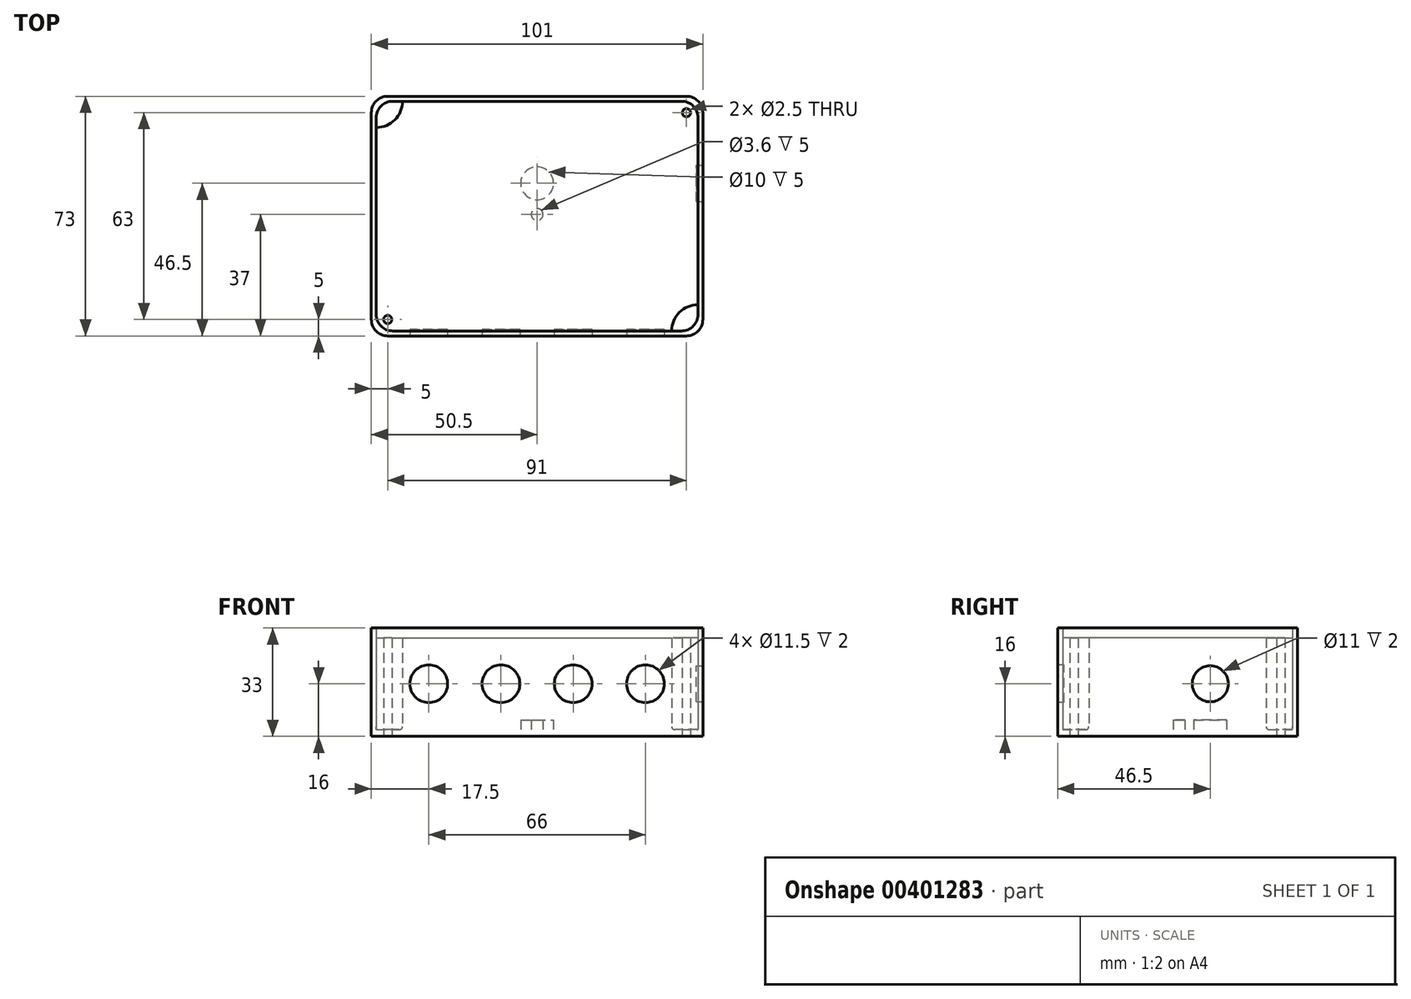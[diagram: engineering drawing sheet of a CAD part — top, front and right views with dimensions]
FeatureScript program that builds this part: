
annotation { "Feature Type Name" : "Feature", "Feature Type Description" : "" }
export const myFeature = defineFeature(function(context is Context, id is Id, definition is map)
    precondition{}
    {
        {
            var Q0;
            Q0=qCreatedBy(makeId("Top.planeOp"),FACE);
            var sketch = newSketch(context, id + "F0", { "sketchPlane" : qUnion([Q0])});
            skLineSegment(sketch, "E0.bottom", {"start": v(49, -45) * mm, "end": v(-49, -45) * mm});
            skLineSegment(sketch, "E0.top", {"start": v(49, 25) * mm, "end": v(-49, 25) * mm});
            skLineSegment(sketch, "E0.left", {"start": v(49, -45) * mm, "end": v(49, 25) * mm});
            skLineSegment(sketch, "E0.right", {"start": v(-49, -45) * mm, "end": v(-49, 25) * mm});
            skLineSegment(sketch, "E1.bottom", {"start": v(-50.5, 26.5) * mm, "end": v(50.5, 26.5) * mm});
            skLineSegment(sketch, "E1.top", {"start": v(-50.5, -46.5) * mm, "end": v(50.5, -46.5) * mm});
            skLineSegment(sketch, "E1.left", {"start": v(-50.5, 26.5) * mm, "end": v(-50.5, -46.5) * mm});
            skLineSegment(sketch, "E1.right", {"start": v(50.5, 26.5) * mm, "end": v(50.5, -46.5) * mm});
            skArc(sketch, "E2", {"start": v(-41, 25) * mm, "mid": v(-43.34, 19.34) * mm, "end": v(-49, 17) * mm});
            skArc(sketch, "E3.MirrorCS", {"start": v(41, 25) * mm, "mid": v(43.34, 19.34) * mm, "end": v(49, 17) * mm});
            skLineSegment(sketch, "E4", {"start": v(-73.7, -10) * mm, "end": v(81.7, -10) * mm, "construction": true});
            skPoint(sketch, "E5", {"position": v(49, -10) * mm});
            skArc(sketch, "E6.MirrorCS", {"start": v(-41, -45) * mm, "mid": v(-43.34, -39.34) * mm, "end": v(-49, -37) * mm});
            skArc(sketch, "E7.MirrorCS", {"start": v(41, -45) * mm, "mid": v(43.34, -39.34) * mm, "end": v(49, -37) * mm});
            skCircle(sketch, "E8", {"center": v(-45.5, 21.5) * mm, "radius": 1.25 * mm});
            skCircle(sketch, "E9.MirrorC", {"center": v(45.5, 21.5) * mm, "radius": 1.25 * mm});
            skCircle(sketch, "E10.MirrorC", {"center": v(45.5, -41.5) * mm, "radius": 1.25 * mm});
            skCircle(sketch, "E11.MirrorC", {"center": v(-45.5, -41.5) * mm, "radius": 1.25 * mm});
            skSolve(sketch);
        }
        {
            var Q0;
            Q0=makeQuery(id+"F0.imprint","IMPRINT",FACE,{"disambiguationData":[TD([[makeQuery(id+"F0.imprint","IMPRINT",EDGE,{"derivedFrom":sQuery(id+"F0.wireOp",EDGE,"E0.bottom")}),-1.0]])]});
            var Q1;
            Q1=makeQuery(id+"F0.imprint","IMPRINT",FACE,{"disambiguationData":[TD([[makeQuery(id+"F0.imprint","IMPRINT",EDGE,{"derivedFrom":sQuery(id+"F0.wireOp",EDGE,"Ogz6Qpz2-tZH1-9vVJ-3AU5-A4KMQRxO9mfY.bottom")}),1.0]])]});
            var Q2;
            {var subQ0=sQuery(id+"F0.wireOp",EDGE,"e8d4081c-b40e-46aa-b9e9-f96a25c7d6070.MirrorC");var subQ1=sQuery(id+"F0.wireOp",EDGE,"usMzGdrf-JS18-KNfs-daDR-j57PrwHz9FGL.top");var subQ2=makeQuery(id+"F0.imprint","INTERSECT",VERTEX,{"derivedFrom":[subQ1,subQ0]});Q2=makeQuery(id+"F0.imprint","IMPRINT",FACE,{"disambiguationData":[TD([[makeQuery(id+"F0.imprint","IMPRINT",EDGE,{"disambiguationData":[TD([[subQ2,-1.0]])],"derivedFrom":subQ1}),-1.0]])]});}
            var Q3;
            {var subQ0=sQuery(id+"F0.wireOp",EDGE,"usMzGdrf-JS18-KNfs-daDR-j57PrwHz9FGL.right");var subQ1=sQuery(id+"F0.wireOp",EDGE,"usMzGdrf-JS18-KNfs-daDR-j57PrwHz9FGL.top");var subQ2=makeQuery(id+"F0.imprint","INTERSECT",VERTEX,{"derivedFrom":[subQ1,subQ0]});Q3=makeQuery(id+"F0.imprint","IMPRINT",FACE,{"disambiguationData":[TD([[makeQuery(id+"F0.imprint","IMPRINT",EDGE,{"disambiguationData":[TD([[subQ2,1.0]])],"derivedFrom":subQ1}),-1.0]])]});}
            var Q4;
            {var subQ0=sQuery(id+"F0.wireOp",EDGE,"e8d4081c-b40e-46aa-b9e9-f96a25c7d6070.MirrorC");var subQ1=sQuery(id+"F0.wireOp",EDGE,"usMzGdrf-JS18-KNfs-daDR-j57PrwHz9FGL.top");var subQ2=makeQuery(id+"F0.imprint","INTERSECT",VERTEX,{"derivedFrom":[subQ1,subQ0]});Q4=makeQuery(id+"F0.imprint","IMPRINT",FACE,{"disambiguationData":[TD([[makeQuery(id+"F0.imprint","IMPRINT",EDGE,{"disambiguationData":[TD([[subQ2,-1.0]])],"derivedFrom":subQ1}),1.0]])]});}
            var Q5;
            {var subQ0=sQuery(id+"F0.wireOp",EDGE,"usMzGdrf-JS18-KNfs-daDR-j57PrwHz9FGL.right");var subQ1=sQuery(id+"F0.wireOp",EDGE,"usMzGdrf-JS18-KNfs-daDR-j57PrwHz9FGL.top");var subQ2=makeQuery(id+"F0.imprint","INTERSECT",VERTEX,{"derivedFrom":[subQ1,subQ0]});Q5=makeQuery(id+"F0.imprint","IMPRINT",FACE,{"disambiguationData":[TD([[makeQuery(id+"F0.imprint","IMPRINT",EDGE,{"disambiguationData":[TD([[subQ2,1.0]])],"derivedFrom":subQ1}),1.0]])]});}
            var Q6;
            {var subQ0=sQuery(id+"F0.wireOp",EDGE,"usMzGdrf-JS18-KNfs-daDR-j57PrwHz9FGL.right");var subQ1=sQuery(id+"F0.wireOp",EDGE,"usMzGdrf-JS18-KNfs-daDR-j57PrwHz9FGL.bottom");var subQ2=makeQuery(id+"F0.imprint","INTERSECT",VERTEX,{"derivedFrom":[subQ1,subQ0]});Q6=makeQuery(id+"F0.imprint","IMPRINT",FACE,{"disambiguationData":[TD([[makeQuery(id+"F0.imprint","IMPRINT",EDGE,{"disambiguationData":[TD([[subQ2,1.0]])],"derivedFrom":subQ1}),-1.0]])]});}
            var Q7;
            {var subQ0=sQuery(id+"F0.wireOp",EDGE,"44b00ebe-043b-4d1d-bd37-5f580f74e6f70.MirrorC");var subQ1=sQuery(id+"F0.wireOp",EDGE,"usMzGdrf-JS18-KNfs-daDR-j57PrwHz9FGL.bottom");var subQ2=makeQuery(id+"F0.imprint","INTERSECT",VERTEX,{"derivedFrom":[subQ1,subQ0]});Q7=makeQuery(id+"F0.imprint","IMPRINT",FACE,{"disambiguationData":[TD([[makeQuery(id+"F0.imprint","IMPRINT",EDGE,{"disambiguationData":[TD([[subQ2,-1.0]])],"derivedFrom":subQ1}),-1.0]])]});}
            var Q8;
            {var subQ0=sQuery(id+"F0.wireOp",EDGE,"44b00ebe-043b-4d1d-bd37-5f580f74e6f70.MirrorC");var subQ1=sQuery(id+"F0.wireOp",EDGE,"usMzGdrf-JS18-KNfs-daDR-j57PrwHz9FGL.bottom");var subQ2=makeQuery(id+"F0.imprint","INTERSECT",VERTEX,{"derivedFrom":[subQ1,subQ0]});Q8=makeQuery(id+"F0.imprint","IMPRINT",FACE,{"disambiguationData":[TD([[makeQuery(id+"F0.imprint","IMPRINT",EDGE,{"disambiguationData":[TD([[subQ2,-1.0]])],"derivedFrom":subQ1}),1.0]])]});}
            var Q9;
            {var subQ0=sQuery(id+"F0.wireOp",EDGE,"usMzGdrf-JS18-KNfs-daDR-j57PrwHz9FGL.right");var subQ1=sQuery(id+"F0.wireOp",EDGE,"usMzGdrf-JS18-KNfs-daDR-j57PrwHz9FGL.bottom");var subQ2=makeQuery(id+"F0.imprint","INTERSECT",VERTEX,{"derivedFrom":[subQ1,subQ0]});Q9=makeQuery(id+"F0.imprint","IMPRINT",FACE,{"disambiguationData":[TD([[makeQuery(id+"F0.imprint","IMPRINT",EDGE,{"disambiguationData":[TD([[subQ2,1.0]])],"derivedFrom":subQ1}),1.0]])]});}
            var Q10;
            {var subQ0=sQuery(id+"F0.wireOp",EDGE,"GhtEGfij-EbOE-fe6g-4XEu-vHL9JId5yvzA");var subQ1=sQuery(id+"F0.wireOp",EDGE,"usMzGdrf-JS18-KNfs-daDR-j57PrwHz9FGL.top");var subQ2=makeQuery(id+"F0.imprint","INTERSECT",VERTEX,{"derivedFrom":[subQ1,subQ0]});Q10=makeQuery(id+"F0.imprint","IMPRINT",FACE,{"disambiguationData":[TD([[makeQuery(id+"F0.imprint","IMPRINT",EDGE,{"disambiguationData":[TD([[subQ2,-1.0]])],"derivedFrom":subQ1}),-1.0]])]});}
            var Q11;
            {var subQ0=sQuery(id+"F0.wireOp",EDGE,"usMzGdrf-JS18-KNfs-daDR-j57PrwHz9FGL.left");var subQ1=sQuery(id+"F0.wireOp",EDGE,"usMzGdrf-JS18-KNfs-daDR-j57PrwHz9FGL.top");var subQ2=makeQuery(id+"F0.imprint","INTERSECT",VERTEX,{"derivedFrom":[subQ1,subQ0]});Q11=makeQuery(id+"F0.imprint","IMPRINT",FACE,{"disambiguationData":[TD([[makeQuery(id+"F0.imprint","IMPRINT",EDGE,{"disambiguationData":[TD([[subQ2,-1.0]])],"derivedFrom":subQ1}),-1.0]])]});}
            var Q12;
            {var subQ0=sQuery(id+"F0.wireOp",EDGE,"GhtEGfij-EbOE-fe6g-4XEu-vHL9JId5yvzA");var subQ1=sQuery(id+"F0.wireOp",EDGE,"usMzGdrf-JS18-KNfs-daDR-j57PrwHz9FGL.top");var subQ2=makeQuery(id+"F0.imprint","INTERSECT",VERTEX,{"derivedFrom":[subQ1,subQ0]});Q12=makeQuery(id+"F0.imprint","IMPRINT",FACE,{"disambiguationData":[TD([[makeQuery(id+"F0.imprint","IMPRINT",EDGE,{"disambiguationData":[TD([[subQ2,-1.0]])],"derivedFrom":subQ1}),1.0]])]});}
            var Q13;
            {var subQ0=sQuery(id+"F0.wireOp",EDGE,"usMzGdrf-JS18-KNfs-daDR-j57PrwHz9FGL.left");var subQ1=sQuery(id+"F0.wireOp",EDGE,"usMzGdrf-JS18-KNfs-daDR-j57PrwHz9FGL.top");var subQ2=makeQuery(id+"F0.imprint","INTERSECT",VERTEX,{"derivedFrom":[subQ1,subQ0]});Q13=makeQuery(id+"F0.imprint","IMPRINT",FACE,{"disambiguationData":[TD([[makeQuery(id+"F0.imprint","IMPRINT",EDGE,{"disambiguationData":[TD([[subQ2,-1.0]])],"derivedFrom":subQ1}),1.0]])]});}
            var Q14;
            {var subQ0=sQuery(id+"F0.wireOp",EDGE,"usMzGdrf-JS18-KNfs-daDR-j57PrwHz9FGL.left");var subQ1=sQuery(id+"F0.wireOp",EDGE,"usMzGdrf-JS18-KNfs-daDR-j57PrwHz9FGL.bottom");var subQ2=makeQuery(id+"F0.imprint","INTERSECT",VERTEX,{"derivedFrom":[subQ1,subQ0]});Q14=makeQuery(id+"F0.imprint","IMPRINT",FACE,{"disambiguationData":[TD([[makeQuery(id+"F0.imprint","IMPRINT",EDGE,{"disambiguationData":[TD([[subQ2,-1.0]])],"derivedFrom":subQ1}),-1.0]])]});}
            var Q15;
            {var subQ0=sQuery(id+"F0.wireOp",EDGE,"2b5212c8-91e9-4741-93b7-60bd23c371950.MirrorC");var subQ1=sQuery(id+"F0.wireOp",EDGE,"usMzGdrf-JS18-KNfs-daDR-j57PrwHz9FGL.bottom");var subQ2=makeQuery(id+"F0.imprint","INTERSECT",VERTEX,{"derivedFrom":[subQ1,subQ0]});Q15=makeQuery(id+"F0.imprint","IMPRINT",FACE,{"disambiguationData":[TD([[makeQuery(id+"F0.imprint","IMPRINT",EDGE,{"disambiguationData":[TD([[subQ2,-1.0]])],"derivedFrom":subQ1}),-1.0]])]});}
            var Q16;
            {var subQ0=sQuery(id+"F0.wireOp",EDGE,"2b5212c8-91e9-4741-93b7-60bd23c371950.MirrorC");var subQ1=sQuery(id+"F0.wireOp",EDGE,"usMzGdrf-JS18-KNfs-daDR-j57PrwHz9FGL.bottom");var subQ2=makeQuery(id+"F0.imprint","INTERSECT",VERTEX,{"derivedFrom":[subQ1,subQ0]});Q16=makeQuery(id+"F0.imprint","IMPRINT",FACE,{"disambiguationData":[TD([[makeQuery(id+"F0.imprint","IMPRINT",EDGE,{"disambiguationData":[TD([[subQ2,-1.0]])],"derivedFrom":subQ1}),1.0]])]});}
            var Q17;
            {var subQ0=sQuery(id+"F0.wireOp",EDGE,"usMzGdrf-JS18-KNfs-daDR-j57PrwHz9FGL.left");var subQ1=sQuery(id+"F0.wireOp",EDGE,"usMzGdrf-JS18-KNfs-daDR-j57PrwHz9FGL.bottom");var subQ2=makeQuery(id+"F0.imprint","INTERSECT",VERTEX,{"derivedFrom":[subQ1,subQ0]});Q17=makeQuery(id+"F0.imprint","IMPRINT",FACE,{"disambiguationData":[TD([[makeQuery(id+"F0.imprint","IMPRINT",EDGE,{"disambiguationData":[TD([[subQ2,-1.0]])],"derivedFrom":subQ1}),1.0]])]});}
            var Q18;
            Q18=makeQuery(id+"F0.imprint","IMPRINT",FACE,{"disambiguationData":[TD([[makeQuery(id+"F0.imprint","IMPRINT",EDGE,{"derivedFrom":sQuery(id+"F0.wireOp",EDGE,"yyMTM6wz-js4i-EUDI-ARsr-gkkKsJFZYTGy")}),-1.0]])]});
            var Q19;
            {var subQ3=sQuery(id+"F0.wireOp",EDGE,"E2");Q19=makeQuery(id+"F0.imprint","IMPRINT",FACE,{"disambiguationData":[TD([[makeQuery(id+"F0.imprint","IMPRINT",EDGE,{"derivedFrom":subQ3}),-1.0]])]});}
            var Q20;
            Q20=makeQuery(id+"F0.imprint","IMPRINT",FACE,{"disambiguationData":[TD([[makeQuery(id+"F0.imprint","IMPRINT",EDGE,{"derivedFrom":sQuery(id+"F0.wireOp",EDGE,"E8")}),1.0]])]});
            var Q21;
            {var subQ3=sQuery(id+"F0.wireOp",EDGE,"E3.MirrorCS");Q21=makeQuery(id+"F0.imprint","IMPRINT",FACE,{"disambiguationData":[TD([[makeQuery(id+"F0.imprint","IMPRINT",EDGE,{"derivedFrom":subQ3}),1.0]])]});}
            var Q22;
            Q22=makeQuery(id+"F0.imprint","IMPRINT",FACE,{"disambiguationData":[TD([[makeQuery(id+"F0.imprint","IMPRINT",EDGE,{"derivedFrom":sQuery(id+"F0.wireOp",EDGE,"E9.MirrorC")}),-1.0]])]});
            var Q23;
            Q23=makeQuery(id+"F0.imprint","IMPRINT",FACE,{"disambiguationData":[TD([[makeQuery(id+"F0.imprint","IMPRINT",EDGE,{"derivedFrom":sQuery(id+"F0.wireOp",EDGE,"E10.MirrorC")}),1.0]])]});
            var Q24;
            Q24=makeQuery(id+"F0.imprint","IMPRINT",FACE,{"disambiguationData":[TD([[makeQuery(id+"F0.imprint","IMPRINT",EDGE,{"derivedFrom":sQuery(id+"F0.wireOp",EDGE,"E11.MirrorC")}),-1.0]])]});
            var Q25;
            {var subQ13=sQuery(id+"F0.wireOp",EDGE,"E2");Q25=makeQuery(id+"F0.imprint","IMPRINT",FACE,{"disambiguationData":[TD([[makeQuery(id+"F0.imprint","IMPRINT",EDGE,{"derivedFrom":subQ13}),1.0]])]});}
            var Q26;
            Q26=makeQuery(id+"F0.imprint","IMPRINT",FACE,{"disambiguationData":[TD([[makeQuery(id+"F0.imprint","IMPRINT",EDGE,{"derivedFrom":sQuery(id+"F0.wireOp",EDGE,"Ogz6Qpz2-tZH1-9vVJ-3AU5-A4KMQRxO9mfY.bottom")}),-1.0]])]});
            extrude(context, id + "F1", {"entities" : qUnion([Q0, Q1, Q2, Q3, Q4, Q5, Q6, Q7, Q8, Q9, Q10, Q11, Q12, Q13, Q14, Q15, Q16, Q17, Q18, Q19, Q20, Q21, Q22, Q23, Q24, Q25, Q26]), "offsetDistance" : 25 * mm, "depth" : 2 * mm});
        }
        {
            var Q0;
            Q0=qSketchRegion(id+"F0",true);
            var Q1;
            {var subQ3=sQuery(id+"F0.wireOp",EDGE,"E6.MirrorCS");Q1=makeQuery(id+"F0.imprint","IMPRINT",FACE,{"disambiguationData":[TD([[makeQuery(id+"F0.imprint","IMPRINT",EDGE,{"derivedFrom":subQ3}),1.0]])]});}
            var Q2;
            {var subQ3=sQuery(id+"F0.wireOp",EDGE,"E7.MirrorCS");Q2=makeQuery(id+"F0.imprint","IMPRINT",FACE,{"disambiguationData":[TD([[makeQuery(id+"F0.imprint","IMPRINT",EDGE,{"derivedFrom":subQ3}),-1.0]])]});}
            var Q3;
            {var subQ3=sQuery(id+"F0.wireOp",EDGE,"E3.MirrorCS");Q3=makeQuery(id+"F0.imprint","IMPRINT",FACE,{"disambiguationData":[TD([[makeQuery(id+"F0.imprint","IMPRINT",EDGE,{"derivedFrom":subQ3}),1.0]])]});}
            var Q4;
            {var subQ3=sQuery(id+"F0.wireOp",EDGE,"E2");Q4=makeQuery(id+"F0.imprint","IMPRINT",FACE,{"disambiguationData":[TD([[makeQuery(id+"F0.imprint","IMPRINT",EDGE,{"derivedFrom":subQ3}),-1.0]])]});}
            extrude(context, id + "F2", {"entities" : qUnion([Q0, Q1, Q2, Q3, Q4]), "operationType" : NewBodyOperationType.ADD, "depth" : 30 * mm});
        }
        {
            var Q0;
            Q0=makeQuery(id+"F0.imprint","IMPRINT",FACE,{"disambiguationData":[TD([[makeQuery(id+"F0.imprint","IMPRINT",EDGE,{"derivedFrom":sQuery(id+"F0.wireOp",EDGE,"E0.bottom")}),1.0]])]});
            extrude(context, id + "F3", {"entities" : qUnion([Q0]), "operationType" : NewBodyOperationType.ADD, "depth" : 33 * mm});
        }
        {
            var Q0;
            Q0=makeQuery(id+"F3.opExtrude","SWEPT_FACE",FACE,{"disambiguationData":[OSD([sQuery(id+"F0.wireOp",EDGE,"E1.right")])]});
            var sketch = newSketch(context, id + "F4", { "sketchPlane" : qUnion([Q0])});
            skLineSegment(sketch, "E12", {"start": v(0, 41.44) * mm, "end": v(0, -27.17) * mm, "construction": true});
            skCircle(sketch, "E13", {"center": v(0, 16) * mm, "radius": 5.5 * mm});
            skSolve(sketch);
        }
        {
            var Q0;
            Q0=makeQuery(id+"F4.imprint","IMPRINT",FACE,{"disambiguationData":[TD([[makeQuery(id+"F4.imprint","IMPRINT",EDGE,{"derivedFrom":sQuery(id+"F4.wireOp",EDGE,"E13")}),1.0]])]});
            extrude(context, id + "F5", {"entities" : qUnion([Q0]), "operationType" : NewBodyOperationType.REMOVE, "oppositeDirection" : true, "offsetDistance" : 25 * mm, "depth" : 2 * mm});
        }
        {
            var Q0;
            Q0=makeQuery(id+"F3.opExtrude","SWEPT_FACE",FACE,{"disambiguationData":[OSD([sQuery(id+"F0.wireOp",EDGE,"E1.top")])]});
            var sketch = newSketch(context, id + "F6", { "sketchPlane" : qUnion([Q0])});
            skLineSegment(sketch, "E14", {"start": v(-97.1, 16) * mm, "end": v(97.5, 16) * mm, "construction": true});
            skCircle(sketch, "E15", {"center": v(-33, 16) * mm, "radius": 5.75 * mm});
            skCircle(sketch, "E16.1.0.0", {"center": v(-11, 16) * mm, "radius": 5.75 * mm});
            skCircle(sketch, "E16.2.0.0", {"center": v(11, 16) * mm, "radius": 5.75 * mm});
            skCircle(sketch, "E16.3.0.0", {"center": v(33, 16) * mm, "radius": 5.75 * mm});
            skLineSegment(sketch, "E16.direction1", {"start": v(-33, 16) * mm, "end": v(-11, 16) * mm, "construction": true});
            skSolve(sketch);
        }
        {
            var Q0;
            Q0=makeQuery(id+"F6.imprint","IMPRINT",FACE,{"disambiguationData":[TD([[makeQuery(id+"F6.imprint","IMPRINT",EDGE,{"derivedFrom":sQuery(id+"F6.wireOp",EDGE,"E15")}),1.0]])]});
            var Q1;
            Q1=makeQuery(id+"F6.imprint","IMPRINT",FACE,{"disambiguationData":[TD([[makeQuery(id+"F6.imprint","IMPRINT",EDGE,{"derivedFrom":sQuery(id+"F6.wireOp",EDGE,"E16.1.0.0")}),1.0]])]});
            var Q2;
            Q2=makeQuery(id+"F6.imprint","IMPRINT",FACE,{"disambiguationData":[TD([[makeQuery(id+"F6.imprint","IMPRINT",EDGE,{"derivedFrom":sQuery(id+"F6.wireOp",EDGE,"E16.2.0.0")}),1.0]])]});
            var Q3;
            Q3=makeQuery(id+"F6.imprint","IMPRINT",FACE,{"disambiguationData":[TD([[makeQuery(id+"F6.imprint","IMPRINT",EDGE,{"derivedFrom":sQuery(id+"F6.wireOp",EDGE,"E16.3.0.0")}),1.0]])]});
            extrude(context, id + "F7", {"entities" : qUnion([Q0, Q1, Q2, Q3]), "operationType" : NewBodyOperationType.REMOVE, "oppositeDirection" : true, "offsetDistance" : 25 * mm, "depth" : 2 * mm});
        }
        {
            var Q0;
            Q0=makeQuery(id+"F1.opExtrude","CAP_EDGE",EDGE,{"disambiguationData":[OSD([sQuery(id+"F0.wireOp",EDGE,"E0.bottom")])],"isStart":false});
            var Q1;
            Q1=makeQuery(id+"F1.opExtrude","CAP_EDGE",EDGE,{"disambiguationData":[OSD([sQuery(id+"F0.wireOp",EDGE,"E0.right")])],"isStart":false});
            var Q2;
            Q2=makeQuery(id+"F1.opExtrude","CAP_EDGE",EDGE,{"disambiguationData":[OSD([sQuery(id+"F0.wireOp",EDGE,"E0.top")])],"isStart":false});
            var Q3;
            Q3=makeQuery(id+"F1.opExtrude","CAP_EDGE",EDGE,{"disambiguationData":[OSD([sQuery(id+"F0.wireOp",EDGE,"E0.left")])],"isStart":false});
            var Q4;
            Q4=makeQuery(id+"F2.boolean.opBoolean","INTERSECT",EDGE,{"derivedFrom":[makeQuery(id+"F1.opExtrude","CAP_FACE",FACE,{"disambiguationData":[OSD([sQuery(id+"F0.wireOp",EDGE,"E0.bottom"),sQuery(id+"F0.wireOp",EDGE,"E0.top"),sQuery(id+"F0.wireOp",EDGE,"E0.left"),sQuery(id+"F0.wireOp",EDGE,"E0.right")])],"isStart":false}),makeQuery(id+"F2.opExtrude","SWEPT_FACE",FACE,{"disambiguationData":[OSD([sQuery(id+"F0.wireOp",EDGE,"E7.MirrorCS")])]})]});
            var Q5;
            Q5=makeQuery(id+"F2.boolean.opBoolean","INTERSECT",EDGE,{"derivedFrom":[makeQuery(id+"F1.opExtrude","CAP_FACE",FACE,{"disambiguationData":[OSD([sQuery(id+"F0.wireOp",EDGE,"E0.bottom"),sQuery(id+"F0.wireOp",EDGE,"E0.top"),sQuery(id+"F0.wireOp",EDGE,"E0.left"),sQuery(id+"F0.wireOp",EDGE,"E0.right")])],"isStart":false}),makeQuery(id+"F2.opExtrude","SWEPT_FACE",FACE,{"disambiguationData":[OSD([sQuery(id+"F0.wireOp",EDGE,"E3.MirrorCS")])]})]});
            var Q6;
            Q6=makeQuery(id+"F2.boolean.opBoolean","INTERSECT",EDGE,{"derivedFrom":[makeQuery(id+"F1.opExtrude","CAP_FACE",FACE,{"disambiguationData":[OSD([sQuery(id+"F0.wireOp",EDGE,"E0.bottom"),sQuery(id+"F0.wireOp",EDGE,"E0.top"),sQuery(id+"F0.wireOp",EDGE,"E0.left"),sQuery(id+"F0.wireOp",EDGE,"E0.right")])],"isStart":false}),makeQuery(id+"F2.opExtrude","SWEPT_FACE",FACE,{"disambiguationData":[OSD([sQuery(id+"F0.wireOp",EDGE,"E2")])]})]});
            var Q7;
            Q7=makeQuery(id+"F2.boolean.opBoolean","INTERSECT",EDGE,{"derivedFrom":[makeQuery(id+"F1.opExtrude","CAP_FACE",FACE,{"disambiguationData":[OSD([sQuery(id+"F0.wireOp",EDGE,"E0.bottom"),sQuery(id+"F0.wireOp",EDGE,"E0.top"),sQuery(id+"F0.wireOp",EDGE,"E0.left"),sQuery(id+"F0.wireOp",EDGE,"E0.right")])],"isStart":false}),makeQuery(id+"F2.opExtrude","SWEPT_FACE",FACE,{"disambiguationData":[OSD([sQuery(id+"F0.wireOp",EDGE,"E6.MirrorCS")])]})]});
            fillet(context, id + "F8", {"entities" : qUnion([Q0, Q1, Q2, Q3, Q4, Q5, Q6, Q7]), "radius" : 1 * mm, "tangentPropagation" : true, "defaultsChanged" : false, "vertexSettings" : [], "allowEdgeOverflow" : false});
        }
        {
            var Q0;
            {var subQ0=sQuery(id+"F0.wireOp",EDGE,"E1.left");var subQ1=sQuery(id+"F0.wireOp",EDGE,"E1.bottom");Q0=makeQuery(id+"F3.boolean.opBoolean","MERGE",EDGE,{"derivedFrom":[makeQuery(id+"F2.opExtrude","SWEPT_EDGE",EDGE,{"disambiguationData":[OSD([subQ1,subQ0])]}),makeQuery(id+"F3.opExtrude","SWEPT_EDGE",EDGE,{"disambiguationData":[OSD([subQ1,subQ0])]})]});}
            var Q1;
            {var subQ0=sQuery(id+"F0.wireOp",EDGE,"E1.right");var subQ1=sQuery(id+"F0.wireOp",EDGE,"E1.bottom");Q1=makeQuery(id+"F3.boolean.opBoolean","MERGE",EDGE,{"derivedFrom":[makeQuery(id+"F2.opExtrude","SWEPT_EDGE",EDGE,{"disambiguationData":[OSD([subQ1,subQ0])]}),makeQuery(id+"F3.opExtrude","SWEPT_EDGE",EDGE,{"disambiguationData":[OSD([subQ1,subQ0])]})]});}
            var Q2;
            {var subQ0=sQuery(id+"F0.wireOp",EDGE,"E1.right");var subQ1=sQuery(id+"F0.wireOp",EDGE,"E1.top");Q2=makeQuery(id+"F3.boolean.opBoolean","MERGE",EDGE,{"derivedFrom":[makeQuery(id+"F2.opExtrude","SWEPT_EDGE",EDGE,{"disambiguationData":[OSD([subQ1,subQ0])]}),makeQuery(id+"F3.opExtrude","SWEPT_EDGE",EDGE,{"disambiguationData":[OSD([subQ1,subQ0])]})]});}
            var Q3;
            {var subQ0=sQuery(id+"F0.wireOp",EDGE,"E1.left");var subQ1=sQuery(id+"F0.wireOp",EDGE,"E1.top");Q3=makeQuery(id+"F3.boolean.opBoolean","MERGE",EDGE,{"derivedFrom":[makeQuery(id+"F2.opExtrude","SWEPT_EDGE",EDGE,{"disambiguationData":[OSD([subQ1,subQ0])]}),makeQuery(id+"F3.opExtrude","SWEPT_EDGE",EDGE,{"disambiguationData":[OSD([subQ1,subQ0])]})]});}
            var Q4;
            Q4=makeQuery(id+"F3.opExtrude","SWEPT_EDGE",EDGE,{"disambiguationData":[OSD([sQuery(id+"F0.wireOp",EDGE,"E0.bottom"),sQuery(id+"F0.wireOp",EDGE,"E0.left")])]});
            var Q5;
            Q5=makeQuery(id+"F3.opExtrude","SWEPT_EDGE",EDGE,{"disambiguationData":[OSD([sQuery(id+"F0.wireOp",EDGE,"E0.top"),sQuery(id+"F0.wireOp",EDGE,"E0.left")])]});
            var Q6;
            Q6=makeQuery(id+"F3.opExtrude","SWEPT_EDGE",EDGE,{"disambiguationData":[OSD([sQuery(id+"F0.wireOp",EDGE,"E0.top"),sQuery(id+"F0.wireOp",EDGE,"E0.right")])]});
            var Q7;
            Q7=makeQuery(id+"F3.opExtrude","SWEPT_EDGE",EDGE,{"disambiguationData":[OSD([sQuery(id+"F0.wireOp",EDGE,"E0.bottom"),sQuery(id+"F0.wireOp",EDGE,"E0.right")])]});
            fillet(context, id + "F9", {"entities" : qUnion([Q0, Q1, Q2, Q3, Q4, Q5, Q6, Q7]), "radius" : 5 * mm, "tangentPropagation" : true, "allowEdgeOverflow" : false});
        }
        {
            var Q0;
            {var subQ0=sQuery(id+"F0.wireOp",EDGE,"E0.right");var subQ1=sQuery(id+"F0.wireOp",EDGE,"E0.left");var subQ2=sQuery(id+"F0.wireOp",EDGE,"E0.top");var subQ3=sQuery(id+"F0.wireOp",EDGE,"E0.bottom");Q0=makeQuery(id+"F2.boolean.opBoolean","MERGE",FACE,{"derivedFrom":[makeQuery(id+"F1.opExtrude","CAP_FACE",FACE,{"disambiguationData":[OSD([subQ3,subQ2,subQ1,subQ0])],"isStart":true}),makeQuery(id+"F2.opExtrude","CAP_FACE",FACE,{"disambiguationData":[OSD([subQ3,subQ2,subQ1,subQ0,sQuery(id+"F0.wireOp",EDGE,"E1.bottom"),sQuery(id+"F0.wireOp",EDGE,"E1.top"),sQuery(id+"F0.wireOp",EDGE,"E1.left"),sQuery(id+"F0.wireOp",EDGE,"E1.right"),sQuery(id+"F0.wireOp",EDGE,"E2"),sQuery(id+"F0.wireOp",EDGE,"E3.MirrorCS"),sQuery(id+"F0.wireOp",EDGE,"E6.MirrorCS"),sQuery(id+"F0.wireOp",EDGE,"E7.MirrorCS"),sQuery(id+"F0.wireOp",EDGE,"E8"),sQuery(id+"F0.wireOp",EDGE,"E9.MirrorC"),sQuery(id+"F0.wireOp",EDGE,"E10.MirrorC"),sQuery(id+"F0.wireOp",EDGE,"E11.MirrorC")])],"isStart":true})]});}
            var sketch = newSketch(context, id + "F10", { "sketchPlane" : qUnion([Q0])});
            skCircle(sketch, "E17", {"center": v(0, 0) * mm, "radius": 5 * mm});
            skCircle(sketch, "E18", {"center": v(0, 9.5) * mm, "radius": 1.8 * mm});
            skSolve(sketch);
        }
        {
            var Q0;
            Q0=makeQuery(id+"F10.imprint","IMPRINT",FACE,{"disambiguationData":[TD([[makeQuery(id+"F10.imprint","IMPRINT",EDGE,{"derivedFrom":sQuery(id+"F10.wireOp",EDGE,"E17")}),1.0]])]});
            var Q1;
            Q1=makeQuery(id+"F10.imprint","IMPRINT",FACE,{"disambiguationData":[TD([[makeQuery(id+"F10.imprint","IMPRINT",EDGE,{"derivedFrom":sQuery(id+"F10.wireOp",EDGE,"E18")}),1.0]])]});
            extrude(context, id + "F11", {"entities" : qUnion([Q0, Q1]), "operationType" : NewBodyOperationType.REMOVE, "oppositeDirection" : true, "depth" : 5 * mm, "offsetDistance" : 25 * mm});
        }
    });
